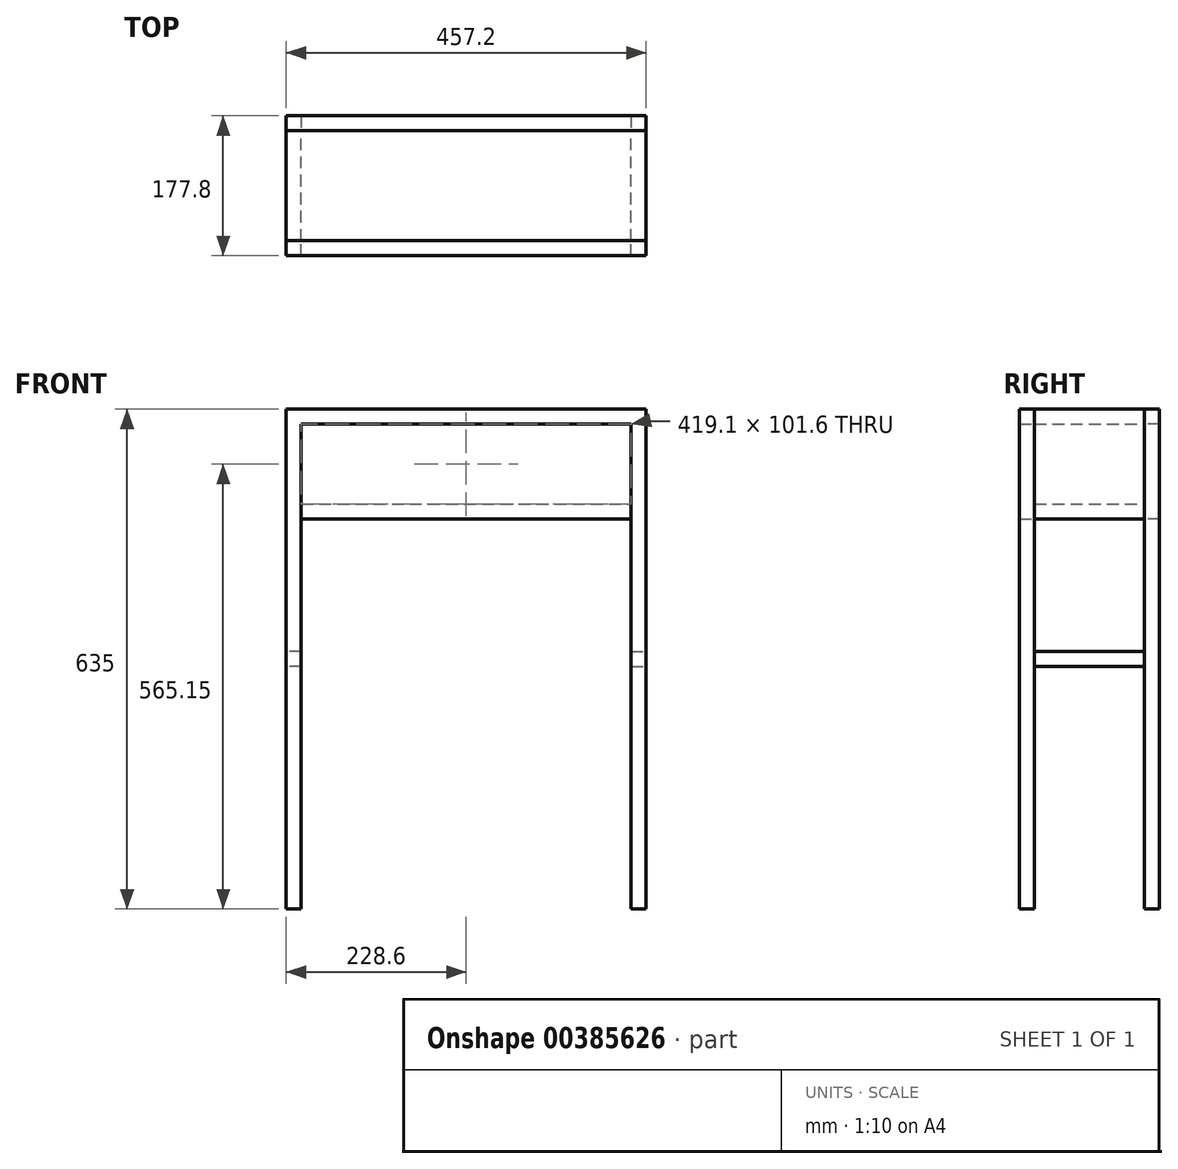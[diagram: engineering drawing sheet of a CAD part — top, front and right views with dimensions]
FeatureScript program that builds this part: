
annotation { "Feature Type Name" : "Feature", "Feature Type Description" : "" }
export const myFeature = defineFeature(function(context is Context, id is Id, definition is map)
    precondition{}
    {
        {
            var Q0;
            Q0=qCreatedBy(makeId("Front.planeOp"),FACE);
            var sketch = newSketch(context, id + "F0", { "sketchPlane" : qUnion([Q0])});
            skLineSegment(sketch, "E0.bottom", {"start": v(-228.6, 69.85) * mm, "end": v(228.6, 69.85) * mm});
            skLineSegment(sketch, "E0.top", {"start": v(-228.6, -69.85) * mm, "end": v(228.6, -69.85) * mm});
            skLineSegment(sketch, "E0.left", {"start": v(-228.6, 69.85) * mm, "end": v(-228.6, -69.85) * mm});
            skLineSegment(sketch, "E0.right", {"start": v(228.6, 69.85) * mm, "end": v(228.6, -69.85) * mm});
            skPoint(sketch, "E0.middle", {"position": v(0, 0) * mm});
            skLineSegment(sketch, "E1.0", {"start": v(-209.55, 50.8) * mm, "end": v(209.55, 50.8) * mm});
            skLineSegment(sketch, "E1.1", {"start": v(-209.55, 50.8) * mm, "end": v(-209.55, -50.8) * mm});
            skLineSegment(sketch, "E1.2", {"start": v(-209.55, -50.8) * mm, "end": v(209.55, -50.8) * mm});
            skLineSegment(sketch, "E1.3", {"start": v(209.55, 50.8) * mm, "end": v(209.55, -50.8) * mm});
            skLineSegment(sketch, "E2", {"start": v(-228.6, 69.85) * mm, "end": v(-209.55, 50.8) * mm});
            skLineSegment(sketch, "E3", {"start": v(-228.6, -69.85) * mm, "end": v(-209.55, -50.8) * mm});
            skLineSegment(sketch, "E4", {"start": v(228.6, -69.85) * mm, "end": v(209.55, -50.8) * mm});
            skLineSegment(sketch, "E5", {"start": v(228.6, 69.85) * mm, "end": v(209.55, 50.8) * mm});
            skSolve(sketch);
        }
        {
            var Q0;
            Q0 = qSketchRegion(id + "F0", true);
            extrude(context, id + "F1", {"entities" : qUnion([Q0]), "endBound" : BoundingType.SYMMETRIC, "depth" : 139.7 * mm, "offsetDistance" : 25 * mm});
        }
        {
            var Q0;
            Q0=makeQuery(id+"F1.opExtrude","CAP_FACE",FACE,{"disambiguationData":[OSD([sQuery(id+"F0.wireOp",EDGE,"E0.bottom"),sQuery(id+"F0.wireOp",EDGE,"E0.top"),sQuery(id+"F0.wireOp",EDGE,"E0.left"),sQuery(id+"F0.wireOp",EDGE,"E0.right"),sQuery(id+"F0.wireOp",EDGE,"E1.0"),sQuery(id+"F0.wireOp",EDGE,"E1.1"),sQuery(id+"F0.wireOp",EDGE,"E1.2"),sQuery(id+"F0.wireOp",EDGE,"E1.3")])],"isStart":true});
            var sketch = newSketch(context, id + "F2", { "sketchPlane" : qUnion([Q0])});
            skLineSegment(sketch, "E6", {"start": v(-228.6, 69.85) * mm, "end": v(228.6, 69.85) * mm});
            skLineSegment(sketch, "E7", {"start": v(228.6, 69.85) * mm, "end": v(209.55, 50.8) * mm});
            skLineSegment(sketch, "E8", {"start": v(209.55, 50.8) * mm, "end": v(-209.55, 50.8) * mm});
            skLineSegment(sketch, "E9", {"start": v(-209.55, 50.8) * mm, "end": v(-228.6, 69.85) * mm});
            skLineSegment(sketch, "E10", {"start": v(-228.6, 69.85) * mm, "end": v(-228.6, -565.15) * mm});
            skLineSegment(sketch, "E11", {"start": v(228.6, 69.85) * mm, "end": v(228.6, -565.15) * mm});
            skLineSegment(sketch, "E12", {"start": v(228.6, -565.15) * mm, "end": v(209.55, -565.15) * mm});
            skLineSegment(sketch, "E13", {"start": v(209.55, -565.15) * mm, "end": v(209.55, 50.8) * mm});
            skLineSegment(sketch, "E14", {"start": v(-209.55, 50.8) * mm, "end": v(-209.55, -565.15) * mm});
            skLineSegment(sketch, "E15", {"start": v(-209.55, -565.15) * mm, "end": v(-228.6, -565.15) * mm});
            skSolve(sketch);
        }
        {
            var Q0;
            Q0 = qSketchRegion(id + "F2", true);
            extrude(context, id + "F3", {"entities" : qUnion([Q0]), "depth" : 19.05 * mm, "offsetDistance" : 25 * mm});
        }
        {
            var Q0;
            Q0=makeQuery(id+"F3.opExtrude","SWEPT_BODY",BODY,{"disambiguationData":[OSD([sQuery(id+"F2.wireOp",EDGE,"E6"),sQuery(id+"F2.wireOp",EDGE,"E8"),sQuery(id+"F2.wireOp",EDGE,"E10"),sQuery(id+"F2.wireOp",EDGE,"E11"),sQuery(id+"F2.wireOp",EDGE,"E12"),sQuery(id+"F2.wireOp",EDGE,"E13"),sQuery(id+"F2.wireOp",EDGE,"E14"),sQuery(id+"F2.wireOp",EDGE,"E15")])]});
            var Q1;
            Q1=qCreatedBy(makeId("Front.planeOp"),FACE);
            mirror(context, id + "F4", {"entities" : qUnion([Q0]), "mirrorPlane" : qUnion([Q1])});
        }
        {
            var Q0;
            Q0=makeQuery(id+"F1.opExtrude","CAP_FACE",FACE,{"disambiguationData":[OSD([sQuery(id+"F0.wireOp",EDGE,"E0.bottom"),sQuery(id+"F0.wireOp",EDGE,"E0.top"),sQuery(id+"F0.wireOp",EDGE,"E0.left"),sQuery(id+"F0.wireOp",EDGE,"E0.right"),sQuery(id+"F0.wireOp",EDGE,"E1.0"),sQuery(id+"F0.wireOp",EDGE,"E1.1"),sQuery(id+"F0.wireOp",EDGE,"E1.2"),sQuery(id+"F0.wireOp",EDGE,"E1.3")])],"isStart":false});
            var sketch = newSketch(context, id + "F5", { "sketchPlane" : qUnion([Q0])});
            skLineSegment(sketch, "E16.0", {"start": v(209.55, 50.8) * mm, "end": v(209.55, -565.15) * mm});
            skLineSegment(sketch, "E17.bottom", {"start": v(-209.55, 50.8) * mm, "end": v(209.55, 50.8) * mm});
            skLineSegment(sketch, "E17.top", {"start": v(-209.55, -69.85) * mm, "end": v(209.55, -69.85) * mm});
            skLineSegment(sketch, "E17.left", {"start": v(-209.55, 50.8) * mm, "end": v(-209.55, -69.85) * mm});
            skLineSegment(sketch, "E17.right", {"start": v(209.55, 50.8) * mm, "end": v(209.55, -69.85) * mm});
            skSolve(sketch);
        }
        {
            var Q0;
            Q0 = qSketchRegion(id + "F5", true);
            extrude(context, id + "F6", {"entities" : qUnion([Q0]), "depth" : 19.05 * mm, "offsetDistance" : 25 * mm});
        }
        {
            var Q0;
            Q0=makeQuery(id+"F6.opExtrude","SWEPT_BODY",BODY,{"disambiguationData":[OSD([sQuery(id+"F5.wireOp",EDGE,"E17.bottom"),sQuery(id+"F5.wireOp",EDGE,"E17.top"),sQuery(id+"F5.wireOp",EDGE,"E17.left"),sQuery(id+"F5.wireOp",EDGE,"E17.right")])]});
            var Q1;
            Q1=qCreatedBy(makeId("Front.planeOp"),FACE);
            mirror(context, id + "F7", {"entities" : qUnion([Q0]), "mirrorPlane" : qUnion([Q1])});
        }
        {
            var Q0;
            Q0=makeQuery(id+"F3.opExtrude","CAP_FACE",FACE,{"disambiguationData":[OSD([sQuery(id+"F2.wireOp",EDGE,"E6"),sQuery(id+"F2.wireOp",EDGE,"E8"),sQuery(id+"F2.wireOp",EDGE,"E10"),sQuery(id+"F2.wireOp",EDGE,"E11"),sQuery(id+"F2.wireOp",EDGE,"E12"),sQuery(id+"F2.wireOp",EDGE,"E13"),sQuery(id+"F2.wireOp",EDGE,"E14"),sQuery(id+"F2.wireOp",EDGE,"E15")])],"isStart":true});
            var sketch = newSketch(context, id + "F8", { "sketchPlane" : qUnion([Q0])});
            skLineSegment(sketch, "E18.bottom", {"start": v(209.55, -257.18) * mm, "end": v(228.6, -257.18) * mm});
            skLineSegment(sketch, "E18.top", {"start": v(209.55, -238.13) * mm, "end": v(228.6, -238.13) * mm});
            skLineSegment(sketch, "E18.left", {"start": v(209.55, -257.18) * mm, "end": v(209.55, -238.13) * mm});
            skLineSegment(sketch, "E18.right", {"start": v(228.6, -257.18) * mm, "end": v(228.6, -238.13) * mm});
            skSolve(sketch);
        }
        {
            var Q0;
            Q0=makeQuery(id+"F8.imprint","IMPRINT",FACE,{"disambiguationData":[TD([[makeQuery(id+"F8.imprint","IMPRINT",EDGE,{"derivedFrom":sQuery(id+"F8.wireOp",EDGE,"E18.bottom")}),1.0]])]});
            var Q1;
            Q1=makeQuery(id+"F4.opPattern","COPY",FACE,{"derivedFrom":makeQuery(id+"F3.opExtrude","CAP_FACE",FACE,{"disambiguationData":[OSD([sQuery(id+"F2.wireOp",EDGE,"E6"),sQuery(id+"F2.wireOp",EDGE,"E8"),sQuery(id+"F2.wireOp",EDGE,"E10"),sQuery(id+"F2.wireOp",EDGE,"E11"),sQuery(id+"F2.wireOp",EDGE,"E12"),sQuery(id+"F2.wireOp",EDGE,"E13"),sQuery(id+"F2.wireOp",EDGE,"E14"),sQuery(id+"F2.wireOp",EDGE,"E15")])],"isStart":true}),"instanceName":"1"});
            extrude(context, id + "F9", {"entities" : qUnion([Q0]), "operationType" : NewBodyOperationType.ADD, "endBound" : BoundingType.UP_TO_SURFACE, "depth" : 25 * mm, "endBoundEntityFace" : qUnion([Q1]), "offsetDistance" : 25 * mm});
        }
        {
            var Q0;
            Q0=makeQuery(id+"F3.opExtrude","SWEPT_BODY",BODY,{"disambiguationData":[OSD([sQuery(id+"F2.wireOp",EDGE,"E6"),sQuery(id+"F2.wireOp",EDGE,"E8"),sQuery(id+"F2.wireOp",EDGE,"E10"),sQuery(id+"F2.wireOp",EDGE,"E11"),sQuery(id+"F2.wireOp",EDGE,"E12"),sQuery(id+"F2.wireOp",EDGE,"E13"),sQuery(id+"F2.wireOp",EDGE,"E14"),sQuery(id+"F2.wireOp",EDGE,"E15")])]});
            var Q1;
            Q1=qCreatedBy(makeId("Right.planeOp"),FACE);
            mirror(context, id + "F10", {"entities" : qUnion([Q0]), "mirrorPlane" : qUnion([Q1])});
        }
    });
